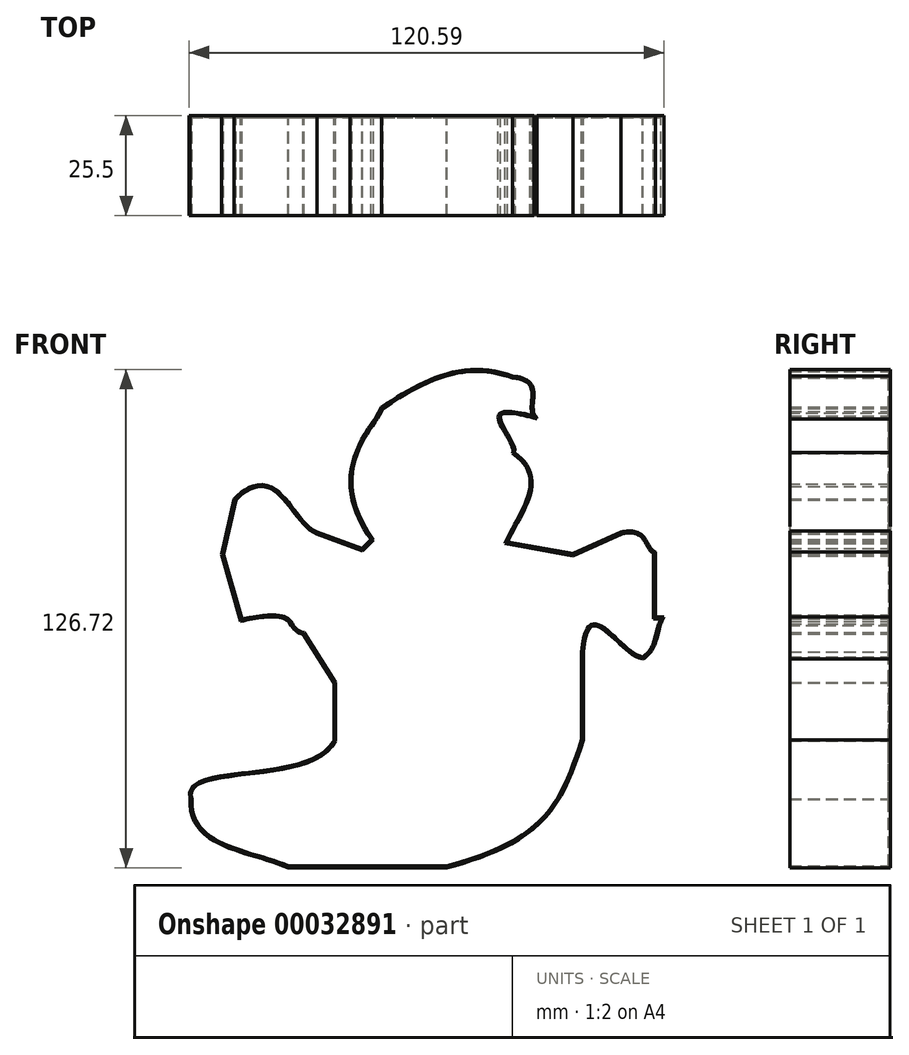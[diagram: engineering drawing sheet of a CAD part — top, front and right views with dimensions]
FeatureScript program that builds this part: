
annotation { "Feature Type Name" : "Feature", "Feature Type Description" : "" }
export const myFeature = defineFeature(function(context is Context, id is Id, definition is map)
    precondition{}
    {
        {
            var Q0;
            Q0=qCreatedBy(makeId("Front.planeOp"),FACE);
            var sketch = newSketch(context, id + "F0", { "sketchPlane" : qUnion([Q0])});
            skLineSegment(sketch, "E0", {"start": v(34.32, -16.54) * mm, "end": v(34.32, -38.8) * mm});
            skLineSegment(sketch, "E1", {"start": v(-28.14, -39.12) * mm, "end": v(-28.14, -24.27) * mm});
            skLineSegment(sketch, "E2", {"start": v(52.57, 8.5) * mm, "end": v(52.57, -8.2) * mm});
            skLineSegment(sketch, "E3", {"start": v(52.57, -8.2) * mm, "end": v(54.42, -8.2) * mm});
            skLineSegment(sketch, "E4", {"start": v(-56.59, 8.2) * mm, "end": v(-51.95, -8.2) * mm});
            skLineSegment(sketch, "E5", {"start": v(-40.2, -70.97) * mm, "end": v(0, -70.97) * mm});
            skLineSegment(sketch, "E6", {"start": v(32.16, 7.89) * mm, "end": v(44.53, 13.45) * mm});
            skLineSegment(sketch, "E7", {"start": v(-21.34, 9.12) * mm, "end": v(-33.09, 13.45) * mm});
            skLineSegment(sketch, "E8", {"start": v(-33.09, 13.45) * mm, "end": v(-33.09, 11.6) * mm});
            skFitSpline(sketch, "E9", {"points": [v(0, -70.97) * mm, v(34.32, -38.8) * mm], "startDerivative": vector(74.23, 20.4) * mm, "endDerivative": vector(16.68, 51.02) * mm});
            skFitSpline(sketch, "E10", {"points": [v(-40.2, -70.97) * mm, v(-64.63, -53.96) * mm], "startDerivative": vector(-25.05, 12.06) * mm, "endDerivative": vector(2.79, 37.1) * mm});
            skFitSpline(sketch, "E11", {"points": [v(-64.63, -53.96) * mm, v(-28.14, -39.12) * mm], "startDerivative": vector(-10.21, 27.83) * mm, "endDerivative": vector(17.62, 36.18) * mm});
            skFitSpline(sketch, "E12", {"points": [v(-28.14, -24.27) * mm, v(-36.18, -11.6) * mm], "startDerivative": vector(-8.04, 12.68) * mm, "endDerivative": vector(-8.04, 12.68) * mm});
            skFitSpline(sketch, "E13", {"points": [v(-36.18, -11.6) * mm, v(-51.95, -8.2) * mm], "startDerivative": vector(-15.77, 3.4) * mm, "endDerivative": vector(-47.31, -10.2) * mm});
            skFitSpline(sketch, "E14", {"points": [v(-56.59, 8.2) * mm, v(-53.5, 22.1) * mm], "startDerivative": vector(3.1, 13.91) * mm, "endDerivative": vector(3.1, 13.91) * mm});
            skFitSpline(sketch, "E15", {"points": [v(-53.5, 22.1) * mm, v(-33.09, 13.45) * mm], "startDerivative": vector(31.54, 30.61) * mm, "endDerivative": vector(20.4, -8.66) * mm});
            skFitSpline(sketch, "E16", {"points": [v(-18.55, 11.9) * mm, v(-16.08, 45.3) * mm], "startDerivative": vector(-37.1, 51.95) * mm, "endDerivative": vector(8.34, 17.63) * mm});
            skFitSpline(sketch, "E17", {"points": [v(-16.08, 45.3) * mm, v(16.7, 53.03) * mm], "startDerivative": vector(48.24, 33.4) * mm, "endDerivative": vector(23.18, -8.35) * mm});
            skFitSpline(sketch, "E18", {"points": [v(21.95, 43.45) * mm, v(16.7, 33.86) * mm], "startDerivative": vector(-51.94, 13.91) * mm, "endDerivative": vector(-5.26, -9.59) * mm});
            skFitSpline(sketch, "E19", {"points": [v(14.84, 10.98) * mm, v(32.16, 7.89) * mm], "startDerivative": vector(17.32, -3.1) * mm, "endDerivative": vector(17.32, -3.1) * mm});
            skFitSpline(sketch, "E20", {"points": [v(44.53, 13.45) * mm, v(52.57, 8.5) * mm], "startDerivative": vector(19.5, 3.71) * mm, "endDerivative": vector(8.04, -4.95) * mm});
            skFitSpline(sketch, "E21", {"points": [v(54.42, -8.2) * mm, v(49.78, -17.78) * mm], "startDerivative": vector(-4.64, -9.59) * mm, "endDerivative": vector(-10.23, -5.57) * mm});
            skFitSpline(sketch, "E22", {"points": [v(49.78, -17.78) * mm, v(34.32, -16.54) * mm], "startDerivative": vector(-15.46, 1.24) * mm, "endDerivative": vector(-3.73, -49.63) * mm});
            skFitSpline(sketch, "E23", {"points": [v(16.7, 53.03) * mm, v(21.95, 43.45) * mm], "startDerivative": vector(24.13, -1.86) * mm, "endDerivative": vector(5.26, -9.59) * mm});
            skFitSpline(sketch, "E24", {"points": [v(16.7, 33.86) * mm, v(14.84, 10.98) * mm], "startDerivative": vector(29.7, -19.48) * mm, "endDerivative": vector(-8.36, -21.34) * mm});
            skLineSegment(sketch, "E25", {"start": v(-18.55, 11.9) * mm, "end": v(-21.34, 9.12) * mm});
            skSolve(sketch);
        }
        {
            var Q0;
            Q0=makeQuery(id+"F0.imprint","IMPRINT",FACE,{"disambiguationData":[TD([[makeQuery(id+"F0.imprint","IMPRINT",EDGE,{"derivedFrom":sQuery(id+"F0.wireOp",EDGE,"E0")}),-1.0]])]});
            extrude(context, id + "F1", {"entities" : qUnion([Q0]), "depth" : 25 * mm});
        }
        {
            var Q0;
            Q0=makeQuery(id+"F1.opExtrude","CAP_FACE",FACE,{"disambiguationData":[OSD([sQuery(id+"F0.wireOp",EDGE,"E0"),sQuery(id+"F0.wireOp",EDGE,"E1"),sQuery(id+"F0.wireOp",EDGE,"E2"),sQuery(id+"F0.wireOp",EDGE,"E3"),sQuery(id+"F0.wireOp",EDGE,"E4"),sQuery(id+"F0.wireOp",EDGE,"E5"),sQuery(id+"F0.wireOp",EDGE,"E6"),sQuery(id+"F0.wireOp",EDGE,"E7"),sQuery(id+"F0.wireOp",EDGE,"E9"),sQuery(id+"F0.wireOp",EDGE,"E10"),sQuery(id+"F0.wireOp",EDGE,"E11"),sQuery(id+"F0.wireOp",EDGE,"E12"),sQuery(id+"F0.wireOp",EDGE,"E13"),sQuery(id+"F0.wireOp",EDGE,"E14"),sQuery(id+"F0.wireOp",EDGE,"E15"),sQuery(id+"F0.wireOp",EDGE,"E16"),sQuery(id+"F0.wireOp",EDGE,"E17"),sQuery(id+"F0.wireOp",EDGE,"E18"),sQuery(id+"F0.wireOp",EDGE,"E19"),sQuery(id+"F0.wireOp",EDGE,"E20"),sQuery(id+"F0.wireOp",EDGE,"E21"),sQuery(id+"F0.wireOp",EDGE,"E22"),sQuery(id+"F0.wireOp",EDGE,"E23"),sQuery(id+"F0.wireOp",EDGE,"E24"),sQuery(id+"F0.wireOp",EDGE,"E25")])],"isStart":false});
            shell(context, id + "F2", {"entities" : qUnion([Q0]), "thickness" : .5 * mm, "oppositeDirection" : true});
        }
    });
